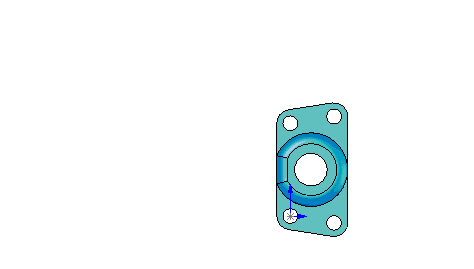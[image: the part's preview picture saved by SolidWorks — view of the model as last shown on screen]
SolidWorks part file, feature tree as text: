
SOLIDWORKS PART (.sldprt)
format: sldprt  version: not decoded by parser v0  size: 160,768 bytes
history: native  units: mm
features: sketch x5, plane x3, cut_extrude x3, extrude x2, material x1, fillet x1 + 1 further entry (+7 scaffold rows collapsed)
feature tree (23):
  scaffold x7  (default folders/planes/origin — collapsed)
  material  "Matériau <non spécifié>"
  "Corps de surface"
  plane  "Face"
  plane  "Dessus"
  plane  "Droite"
  sketch  "Esquisse1"  dims[D2=5.0mm D1=26.0mm D3=2.5mm D4=34.0mm D5=2.5mm]
  extrude  "Extrusion1"  Depth=4mm
  sketch  "Esquisse2"  dims[D1=27.0mm D2=12.5mm D3=17.0mm D4=12.5mm]
  extrude  "Extrusion2"  Depth=5.8mm
  fillet  "Congé1"  Radius=4mm
  sketch  "Esquisse3"  dims[D1=12.0mm]
  cut_extrude  "Enlèv. mat.-Extru.1"  [1 undecoded]
  sketch  "Esquisse4"  dims[D1=19.0mm]
  cut_extrude  "Enlèv. mat.-Extru.2"  Depth=6mm
  sketch  "Esquisse5"  dims[D1=5.5mm D2=5.5mm D3=5.5mm D4=5.5mm]
  cut_extrude  "Enlèv. mat.-Extru.3"  [1 undecoded]
decode coverage: 9 of 11 modeling features carry decoded parameters; 1 rows unclassified (native names shown)
note: 2 parameter values undecoded
note: suppression state not decoded; provenance and decode notes live in map.json
